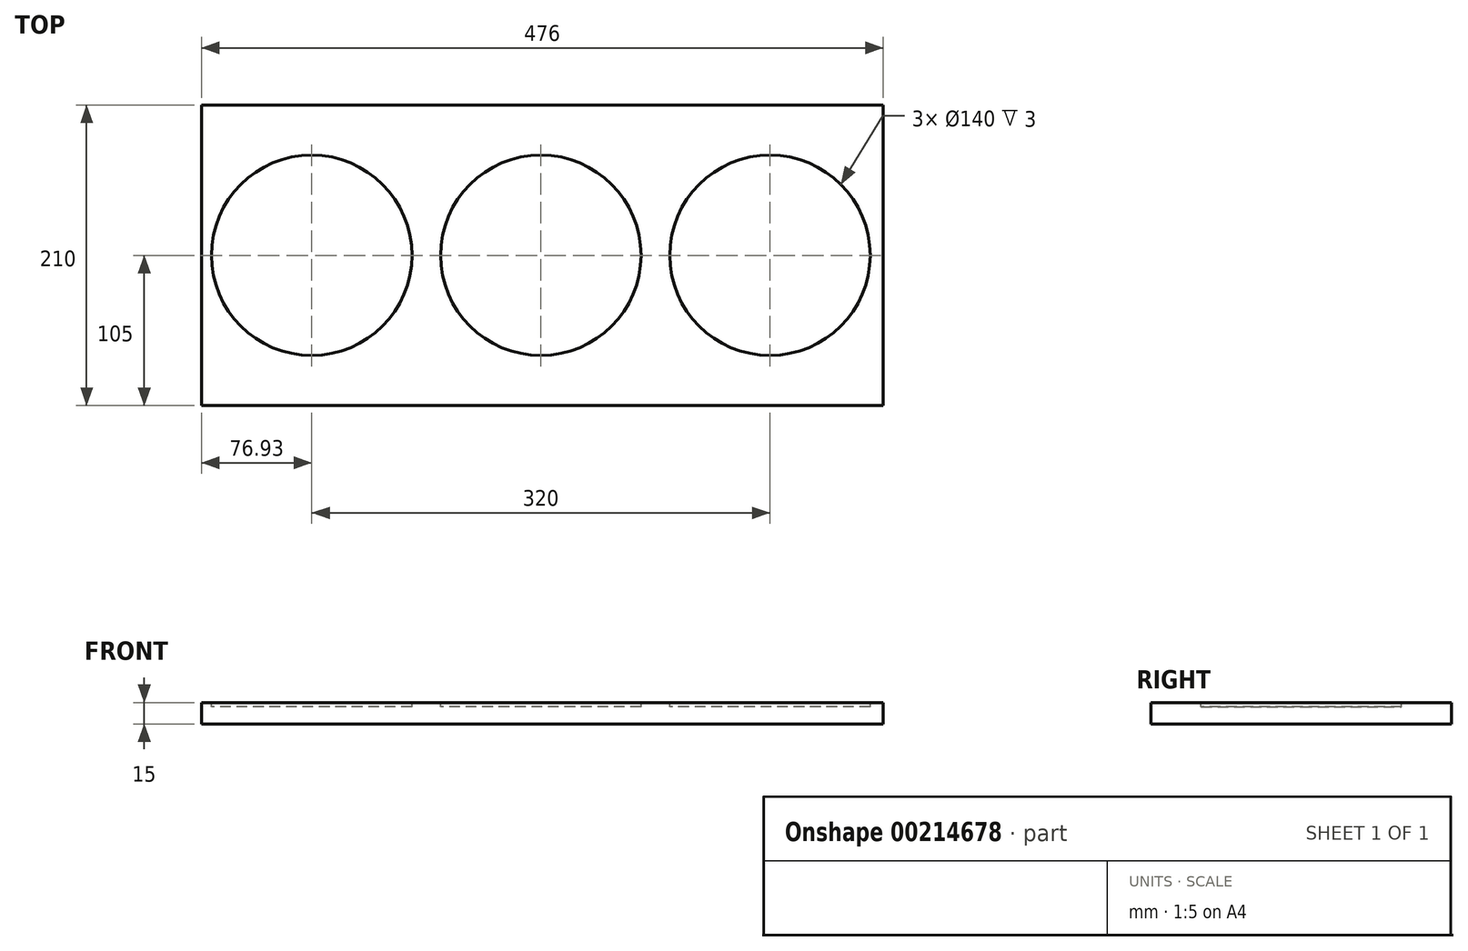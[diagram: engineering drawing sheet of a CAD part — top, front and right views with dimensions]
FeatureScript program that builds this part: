
annotation { "Feature Type Name" : "Feature", "Feature Type Description" : "" }
export const myFeature = defineFeature(function(context is Context, id is Id, definition is map)
    precondition{}
    {
        {
            var Q0;
            Q0=qCreatedBy(makeId("Top.planeOp"),FACE);
            var sketch = newSketch(context, id + "F0", { "sketchPlane" : qUnion([Q0])});
            skLineSegment(sketch, "E0.bottom", {"start": v(-236.93, 105) * mm, "end": v(239.07, 105) * mm});
            skLineSegment(sketch, "E0.top", {"start": v(-236.93, -105) * mm, "end": v(239.07, -105) * mm});
            skLineSegment(sketch, "E0.left", {"start": v(-236.93, 105) * mm, "end": v(-236.93, -105) * mm});
            skLineSegment(sketch, "E0.right", {"start": v(239.07, 105) * mm, "end": v(239.07, -105) * mm});
            skCircle(sketch, "E1", {"center": v(0, 0) * mm, "radius": 70 * mm});
            skCircle(sketch, "E2", {"center": v(160, 0) * mm, "radius": 70 * mm});
            skCircle(sketch, "E3", {"center": v(-160, 0) * mm, "radius": 70 * mm});
            skSolve(sketch);
        }
        {
            var Q0;
            Q0=makeQuery(id+"F0.imprint","IMPRINT",FACE,{"disambiguationData":[TD([[makeQuery(id+"F0.imprint","IMPRINT",EDGE,{"derivedFrom":sQuery(id+"F0.wireOp",EDGE,"E0.bottom")}),-1.0]])]});
            var Q1;
            Q1=makeQuery(id+"F0.imprint","IMPRINT",FACE,{"disambiguationData":[TD([[makeQuery(id+"F0.imprint","IMPRINT",EDGE,{"derivedFrom":sQuery(id+"F0.wireOp",EDGE,"E3")}),1.0]])]});
            var Q2;
            Q2=makeQuery(id+"F0.imprint","IMPRINT",FACE,{"disambiguationData":[TD([[makeQuery(id+"F0.imprint","IMPRINT",EDGE,{"derivedFrom":sQuery(id+"F0.wireOp",EDGE,"E1")}),1.0]])]});
            var Q3;
            Q3=makeQuery(id+"F0.imprint","IMPRINT",FACE,{"disambiguationData":[TD([[makeQuery(id+"F0.imprint","IMPRINT",EDGE,{"derivedFrom":sQuery(id+"F0.wireOp",EDGE,"E2")}),1.0]])]});
            extrude(context, id + "F1", {"entities" : qUnion([Q0, Q1, Q2, Q3]), "oppositeDirection" : true, "depth" : 15 * mm});
        }
        {
            var Q0;
            Q0=makeQuery(id+"F0.imprint","IMPRINT",FACE,{"disambiguationData":[TD([[makeQuery(id+"F0.imprint","IMPRINT",EDGE,{"derivedFrom":sQuery(id+"F0.wireOp",EDGE,"E3")}),1.0]])]});
            var Q1;
            Q1=makeQuery(id+"F0.imprint","IMPRINT",FACE,{"disambiguationData":[TD([[makeQuery(id+"F0.imprint","IMPRINT",EDGE,{"derivedFrom":sQuery(id+"F0.wireOp",EDGE,"E1")}),1.0]])]});
            var Q2;
            Q2=makeQuery(id+"F0.imprint","IMPRINT",FACE,{"disambiguationData":[TD([[makeQuery(id+"F0.imprint","IMPRINT",EDGE,{"derivedFrom":sQuery(id+"F0.wireOp",EDGE,"E2")}),1.0]])]});
            extrude(context, id + "F2", {"entities" : qUnion([Q0, Q1, Q2]), "operationType" : NewBodyOperationType.REMOVE, "oppositeDirection" : true, "depth" : 3 * mm});
        }
        {
            var Q0;
            Q0=makeQuery(id+"F0.imprint","IMPRINT",FACE,{"disambiguationData":[TD([[makeQuery(id+"F0.imprint","IMPRINT",EDGE,{"derivedFrom":sQuery(id+"F0.wireOp",EDGE,"E3")}),1.0]])]});
            var sketch = newSketch(context, id + "F3", { "sketchPlane" : qUnion([Q0])});
            skCircle(sketch, "E4", {"center": v(-190, 0) * mm, "radius": 24 * mm});
            skLineSegment(sketch, "E5", {"start": v(-160, 0) * mm, "end": v(-160, 31.63) * mm});
            skCircle(sketch, "E6.MirrorC", {"center": v(-130, 0) * mm, "radius": 24 * mm});
            skCircle(sketch, "E7", {"center": v(-190, 0) * mm, "radius": 34 * mm});
            skCircle(sketch, "E8.MirrorC", {"center": v(-130, 0) * mm, "radius": 34 * mm});
            skSolve(sketch);
        }
        {
            var Q0;
            Q0=makeQuery(id+"F1.opExtrude","CAP_FACE",FACE,{"disambiguationData":[OSD([sQuery(id+"F0.wireOp",EDGE,"E0.bottom"),sQuery(id+"F0.wireOp",EDGE,"E0.top"),sQuery(id+"F0.wireOp",EDGE,"E0.left"),sQuery(id+"F0.wireOp",EDGE,"E0.right")])],"isStart":false});
            var sketch = newSketch(context, id + "F4", { "sketchPlane" : qUnion([Q0])});
            skLineSegment(sketch, "E9", {"start": v(-130, 0) * mm, "end": v(-130, -36.8) * mm});
            skSolve(sketch);
        }
        {
            var Q0;
            Q0=qCreatedBy(makeId("Right.planeOp"),FACE);
            cPlane(context, id + "F5", {"entities" : qUnion([Q0]), "cplaneType" : CPlaneType.OFFSET, "offset" : 130 * mm, "oppositeDirection" : true, "width" : 150 * mm, "height" : 150 * mm});
        }
        {
            var Q0;
            Q0=qCreatedBy(id+"F5.planeOp",FACE);
            var sketch = newSketch(context, id + "F6", { "sketchPlane" : qUnion([Q0])});
            skLineSegment(sketch, "E10", {"start": v(0, 0) * mm, "end": v(0, -10) * mm});
            skLineSegment(sketch, "E11", {"start": v(0, -10) * mm, "end": v(35, -10) * mm});
            skArc(sketch, "E12", {"start": v(0, -10) * mm, "mid": v(10.54, -35.03) * mm, "end": v(35.8, -45) * mm});
            skLineSegment(sketch, "E13", {"start": v(35.8, -45) * mm, "end": v(135.8, -45) * mm});
            skSolve(sketch);
        }
        {
            var Q0;
            Q0=qCreatedBy(id+"F5.planeOp",FACE);
            cPlane(context, id + "F7", {"entities" : qUnion([Q0]), "cplaneType" : CPlaneType.OFFSET, "offset" : 60 * mm, "oppositeDirection" : true, "width" : 150 * mm, "height" : 150 * mm});
        }
    });
